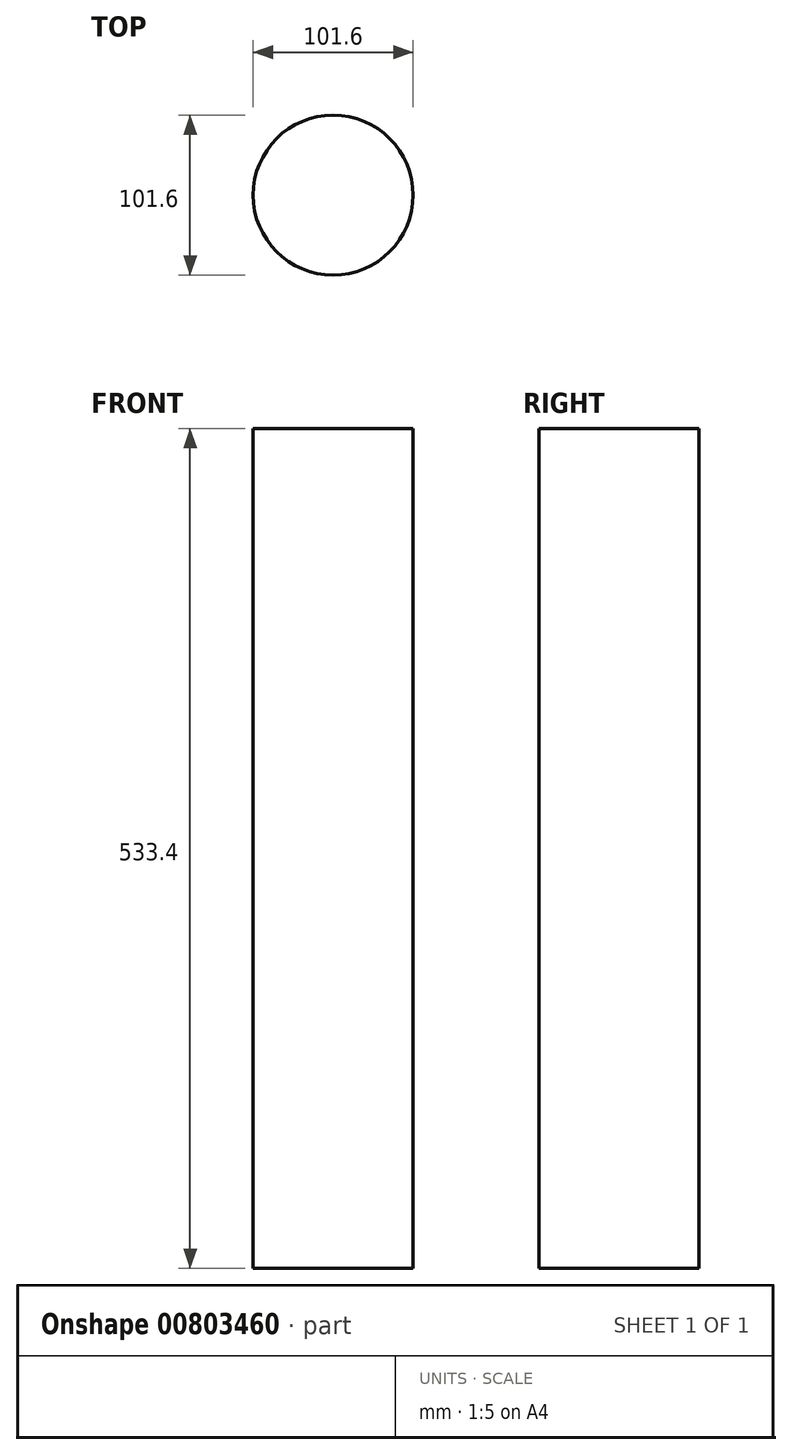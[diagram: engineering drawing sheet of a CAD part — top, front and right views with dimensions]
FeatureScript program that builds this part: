
annotation { "Feature Type Name" : "Feature", "Feature Type Description" : "" }
export const myFeature = defineFeature(function(context is Context, id is Id, definition is map)
    precondition{}
    {
        {
            var Q0;
            Q0=qCreatedBy(makeId("Top.planeOp"),FACE);
            var sketch = newSketch(context, id + "F0", { "sketchPlane" : qUnion([Q0])});
            skCircle(sketch, "E0", {"center": v(0, 0) * mm, "radius": 50.8 * mm});
            skSolve(sketch);
        }
        {
            var Q0;
            Q0=makeQuery(id+"F0.imprint","IMPRINT",FACE,{"disambiguationData":[TD([[makeQuery(id+"F0.imprint","IMPRINT",EDGE,{"derivedFrom":sQuery(id+"F0.wireOp",EDGE,"E0")}),1.0]])]});
            extrude(context, id + "F1", {"entities" : qUnion([Q0]), "endBound" : BoundingType.SYMMETRIC, "depth" : 533.4 * mm, "offsetDistance" : 25.4 * mm});
        }
    });
